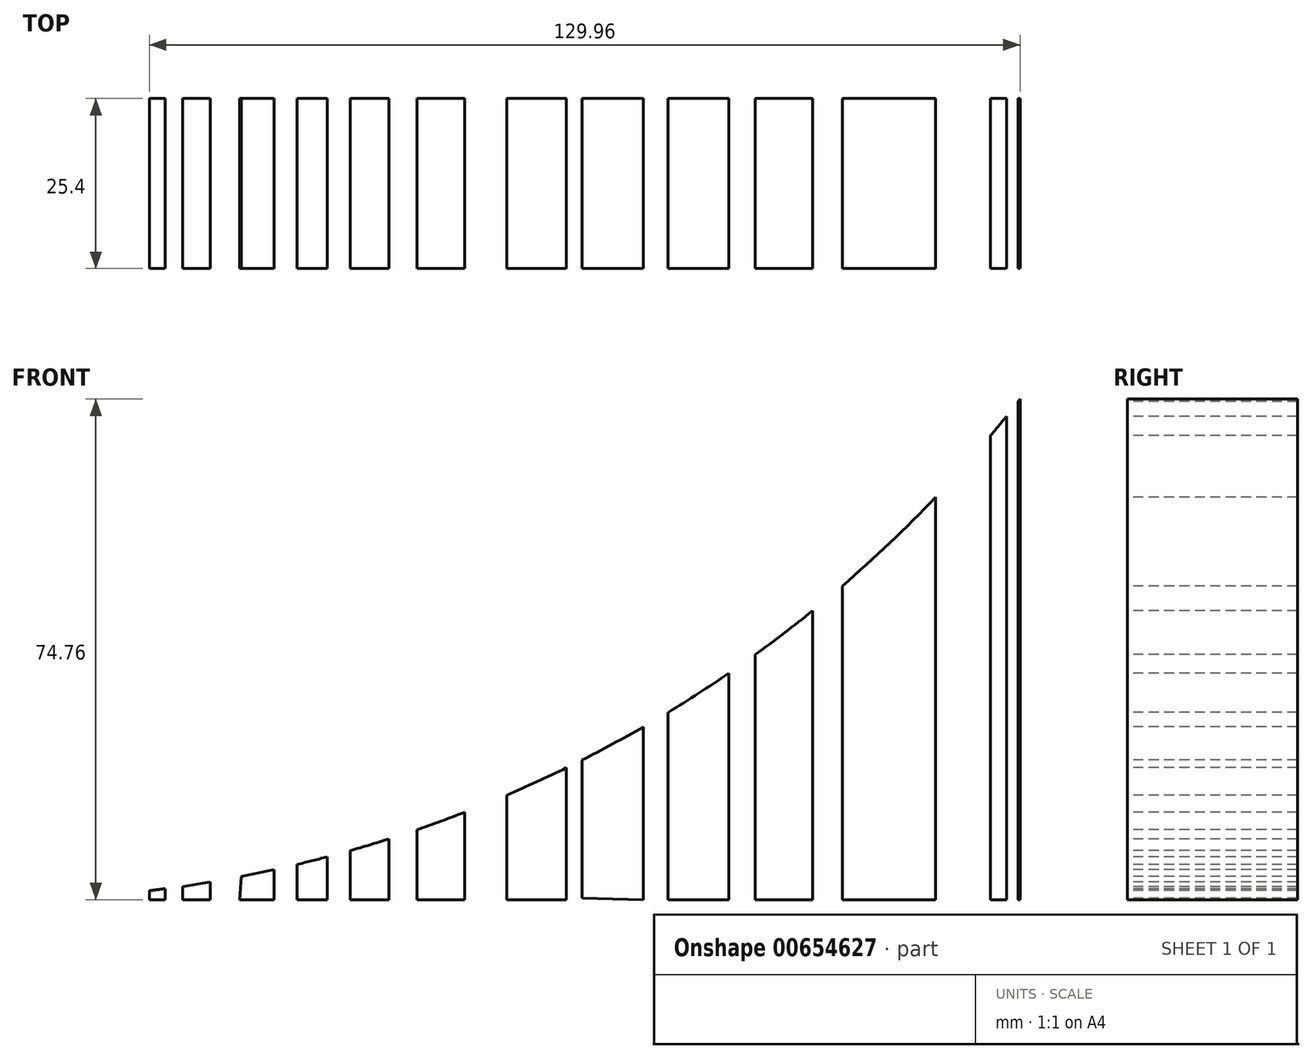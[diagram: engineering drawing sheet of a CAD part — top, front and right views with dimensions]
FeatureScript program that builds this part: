
annotation { "Feature Type Name" : "Feature", "Feature Type Description" : "" }
export const myFeature = defineFeature(function(context is Context, id is Id, definition is map)
    precondition{}
    {
        {
            var Q0;
            Q0=qCreatedBy(makeId("Front.planeOp"),FACE);
            var sketch = newSketch(context, id + "F0", { "sketchPlane" : qUnion([Q0])});
            skLineSegment(sketch, "E0", {"start": v(-76.13, -17.67) * mm, "end": v(76.6, -17.67) * mm});
            skLineSegment(sketch, "E1", {"start": v(76.6, -17.67) * mm, "end": v(76.6, 57.09) * mm});
            skArc(sketch, "E2", {"start": v(-76.13, -17.67) * mm, "mid": v(8.9, 2.02) * mm, "end": v(76.6, 57.09) * mm});
            skSolve(sketch);
        }
        {
            var Q0;
            Q0=makeQuery(id+"F0.imprint","IMPRINT",FACE,{"disambiguationData":[TD([[makeQuery(id+"F0.imprint","IMPRINT",EDGE,{"derivedFrom":sQuery(id+"F0.wireOp",EDGE,"E0")}),1.0]])]});
            extrude(context, id + "F1", {"entities" : qUnion([Q0]), "depth" : 25.4 * mm, "offsetDistance" : 25.4 * mm});
        }
        {
            var Q0;
            Q0=makeQuery(id+"F1.opExtrude","CAP_FACE",FACE,{"disambiguationData":[OSD([sQuery(id+"F0.wireOp",EDGE,"E0"),sQuery(id+"F0.wireOp",EDGE,"E1"),sQuery(id+"F0.wireOp",EDGE,"E2")])],"isStart":false});
            var sketch = newSketch(context, id + "F2", { "sketchPlane" : qUnion([Q0])});
            skLineSegment(sketch, "E3", {"start": v(76.3, 56.71) * mm, "end": v(76.3, -17.67) * mm});
            skLineSegment(sketch, "E4", {"start": v(76.3, -17.67) * mm, "end": v(74.56, -17.67) * mm});
            skLineSegment(sketch, "E5", {"start": v(74.56, -17.67) * mm, "end": v(74.56, 54.51) * mm});
            skLineSegment(sketch, "E6", {"start": v(74.56, 54.51) * mm, "end": v(76.3, 56.71) * mm});
            skLineSegment(sketch, "E7", {"start": v(72.2, 51.63) * mm, "end": v(72.2, -17.67) * mm});
            skLineSegment(sketch, "E8", {"start": v(72.2, -17.67) * mm, "end": v(64, -17.67) * mm});
            skLineSegment(sketch, "E9", {"start": v(64, -17.67) * mm, "end": v(64, 42.45) * mm});
            skLineSegment(sketch, "E10", {"start": v(64, 42.45) * mm, "end": v(65.31, 43.96) * mm});
            skLineSegment(sketch, "E11", {"start": v(50.05, 29.17) * mm, "end": v(50.05, -17.67) * mm});
            skLineSegment(sketch, "E12", {"start": v(50.05, -17.67) * mm, "end": v(48.52, -17.67) * mm});
            skLineSegment(sketch, "E13", {"start": v(48.52, -17.67) * mm, "end": v(48.52, 27.87) * mm});
            skLineSegment(sketch, "E14", {"start": v(48.52, 27.87) * mm, "end": v(50.05, 29.17) * mm});
            skLineSegment(sketch, "E15", {"start": v(45.66, 25.5) * mm, "end": v(45.66, -17.67) * mm});
            skLineSegment(sketch, "E16", {"start": v(45.66, -17.67) * mm, "end": v(37.08, -17.67) * mm});
            skLineSegment(sketch, "E17", {"start": v(37.08, -17.67) * mm, "end": v(37.08, 18.93) * mm});
            skLineSegment(sketch, "E18", {"start": v(37.08, 18.93) * mm, "end": v(45.66, 25.5) * mm});
            skLineSegment(sketch, "E19", {"start": v(33.12, 16.15) * mm, "end": v(33.12, -17.67) * mm});
            skLineSegment(sketch, "E20", {"start": v(33.12, -17.67) * mm, "end": v(24.07, -17.67) * mm});
            skLineSegment(sketch, "E21", {"start": v(24.07, -17.67) * mm, "end": v(24.07, 10.32) * mm});
            skLineSegment(sketch, "E22", {"start": v(24.07, 10.32) * mm, "end": v(33.12, 16.15) * mm});
            skLineSegment(sketch, "E23", {"start": v(20.35, 8.12) * mm, "end": v(20.35, -17.67) * mm});
            skLineSegment(sketch, "E24", {"start": v(20.35, -17.67) * mm, "end": v(11.2, -17.4) * mm});
            skLineSegment(sketch, "E25", {"start": v(11.2, -17.4) * mm, "end": v(11.2, 3.18) * mm});
            skLineSegment(sketch, "E26", {"start": v(11.2, 3.18) * mm, "end": v(20.25, 8.04) * mm});
            skLineSegment(sketch, "E27", {"start": v(8.9, 2.02) * mm, "end": v(8.9, -17.67) * mm});
            skPoint(sketch, "E27.endSnap0", {"position": v(8.9, 2.02) * mm});
            skLineSegment(sketch, "E28", {"start": v(8.9, -17.67) * mm, "end": v(0, -17.67) * mm});
            skLineSegment(sketch, "E29", {"start": v(0, -17.67) * mm, "end": v(0, -2.05) * mm});
            skLineSegment(sketch, "E30", {"start": v(0, -2.05) * mm, "end": v(8.9, 2.02) * mm});
            skLineSegment(sketch, "E31", {"start": v(-6.3, -4.62) * mm, "end": v(-6.3, -17.67) * mm});
            skLineSegment(sketch, "E32", {"start": v(-6.3, -17.67) * mm, "end": v(-13.44, -17.67) * mm});
            skLineSegment(sketch, "E33", {"start": v(-13.44, -17.67) * mm, "end": v(-13.44, -7.23) * mm});
            skLineSegment(sketch, "E34", {"start": v(-13.44, -7.23) * mm, "end": v(-6.3, -4.62) * mm});
            skLineSegment(sketch, "E35", {"start": v(-17.6, -8.6) * mm, "end": v(-17.6, -17.67) * mm});
            skLineSegment(sketch, "E36", {"start": v(-17.6, -17.67) * mm, "end": v(-23.43, -17.67) * mm});
            skLineSegment(sketch, "E37", {"start": v(-23.43, -17.67) * mm, "end": v(-23.43, -10.35) * mm});
            skLineSegment(sketch, "E38", {"start": v(-23.43, -10.35) * mm, "end": v(-17.6, -8.6) * mm});
            skLineSegment(sketch, "E39", {"start": v(-26.84, -11.28) * mm, "end": v(-26.84, -17.67) * mm});
            skLineSegment(sketch, "E40", {"start": v(-26.84, -17.67) * mm, "end": v(-31.33, -17.67) * mm});
            skLineSegment(sketch, "E41", {"start": v(-31.33, -17.67) * mm, "end": v(-31.33, -12.4) * mm});
            skLineSegment(sketch, "E42", {"start": v(-31.33, -12.4) * mm, "end": v(-26.84, -11.28) * mm});
            skLineSegment(sketch, "E43", {"start": v(-34.78, -13.2) * mm, "end": v(-34.78, -17.67) * mm});
            skLineSegment(sketch, "E44", {"start": v(-34.78, -17.67) * mm, "end": v(-39.89, -17.67) * mm});
            skLineSegment(sketch, "E45", {"start": v(-39.89, -17.67) * mm, "end": v(-39.63, -14.17) * mm});
            skLineSegment(sketch, "E46", {"start": v(-39.63, -14.17) * mm, "end": v(-34.78, -13.2) * mm});
            skLineSegment(sketch, "E47", {"start": v(-44.3, -15.03) * mm, "end": v(-44.3, -17.67) * mm});
            skLineSegment(sketch, "E48", {"start": v(-44.3, -17.67) * mm, "end": v(-48.45, -17.67) * mm});
            skLineSegment(sketch, "E49", {"start": v(-48.45, -17.67) * mm, "end": v(-48.45, -15.72) * mm});
            skLineSegment(sketch, "E50", {"start": v(-48.45, -15.72) * mm, "end": v(-44.3, -15.03) * mm});
            skLineSegment(sketch, "E51", {"start": v(-51, -16.03) * mm, "end": v(-51, -17.67) * mm});
            skLineSegment(sketch, "E52", {"start": v(-51, -17.67) * mm, "end": v(-53.37, -17.67) * mm});
            skLineSegment(sketch, "E53", {"start": v(-53.37, -17.67) * mm, "end": v(-53.37, -16.11) * mm});
            skLineSegment(sketch, "E54", {"start": v(-53.37, -16.11) * mm, "end": v(-51, -16.03) * mm});
            skSolve(sketch);
        }
        {
            var Q0;
            {var subQ0=sQuery(id+"F2.wireOp",EDGE,"E11");Q0=makeQuery(id+"F2.imprint","IMPRINT",FACE,{"disambiguationData":[TD([[makeQuery(id+"F2.imprint","IMPRINT",EDGE,{"derivedFrom":subQ0}),-1.0]])]});}
            var Q1;
            {var subQ0=sQuery(id+"F2.wireOp",EDGE,"E7");Q1=makeQuery(id+"F2.imprint","IMPRINT",FACE,{"disambiguationData":[TD([[makeQuery(id+"F2.imprint","IMPRINT",EDGE,{"derivedFrom":subQ0}),-1.0]])]});}
            var Q2;
            {var subQ0=sQuery(id+"F2.wireOp",EDGE,"E3");Q2=makeQuery(id+"F2.imprint","IMPRINT",FACE,{"disambiguationData":[TD([[makeQuery(id+"F2.imprint","IMPRINT",EDGE,{"derivedFrom":subQ0}),-1.0]])]});}
            var Q3;
            {var subQ0=sQuery(id+"F2.wireOp",EDGE,"E13");Q3=makeQuery(id+"F2.imprint","IMPRINT",FACE,{"disambiguationData":[TD([[makeQuery(id+"F2.imprint","IMPRINT",EDGE,{"derivedFrom":subQ0}),1.0]])]});}
            var Q4;
            {var subQ0=sQuery(id+"F2.wireOp",EDGE,"E17");Q4=makeQuery(id+"F2.imprint","IMPRINT",FACE,{"disambiguationData":[TD([[makeQuery(id+"F2.imprint","IMPRINT",EDGE,{"derivedFrom":subQ0}),1.0]])]});}
            var Q5;
            {var subQ0=sQuery(id+"F2.wireOp",EDGE,"E21");Q5=makeQuery(id+"F2.imprint","IMPRINT",FACE,{"disambiguationData":[TD([[makeQuery(id+"F2.imprint","IMPRINT",EDGE,{"derivedFrom":subQ0}),1.0]])]});}
            var Q6;
            {var subQ0=sQuery(id+"F2.wireOp",EDGE,"E24");Q6=makeQuery(id+"F2.imprint","IMPRINT",FACE,{"disambiguationData":[TD([[makeQuery(id+"F2.imprint","IMPRINT",EDGE,{"derivedFrom":subQ0}),1.0]])]});}
            var Q7;
            {var subQ0=sQuery(id+"F2.wireOp",EDGE,"E29");Q7=makeQuery(id+"F2.imprint","IMPRINT",FACE,{"disambiguationData":[TD([[makeQuery(id+"F2.imprint","IMPRINT",EDGE,{"derivedFrom":subQ0}),1.0]])]});}
            var Q8;
            {var subQ0=sQuery(id+"F2.wireOp",EDGE,"E33");Q8=makeQuery(id+"F2.imprint","IMPRINT",FACE,{"disambiguationData":[TD([[makeQuery(id+"F2.imprint","IMPRINT",EDGE,{"derivedFrom":subQ0}),1.0]])]});}
            var Q9;
            {var subQ5=sQuery(id+"F2.wireOp",EDGE,"E39");Q9=makeQuery(id+"F2.imprint","IMPRINT",FACE,{"disambiguationData":[TD([[makeQuery(id+"F2.imprint","IMPRINT",EDGE,{"derivedFrom":subQ5}),1.0]])]});}
            var Q10;
            {var subQ0=sQuery(id+"F2.wireOp",EDGE,"E41");Q10=makeQuery(id+"F2.imprint","IMPRINT",FACE,{"disambiguationData":[TD([[makeQuery(id+"F2.imprint","IMPRINT",EDGE,{"derivedFrom":subQ0}),1.0]])]});}
            var Q11;
            {var subQ5=sQuery(id+"F2.wireOp",EDGE,"E47");Q11=makeQuery(id+"F2.imprint","IMPRINT",FACE,{"disambiguationData":[TD([[makeQuery(id+"F2.imprint","IMPRINT",EDGE,{"derivedFrom":subQ5}),1.0]])]});}
            var Q12;
            {var subQ3=sQuery(id+"F2.wireOp",EDGE,"E49");Q12=makeQuery(id+"F2.imprint","IMPRINT",FACE,{"disambiguationData":[TD([[makeQuery(id+"F2.imprint","IMPRINT",EDGE,{"derivedFrom":subQ3}),1.0]])]});}
            var Q13;
            {var subQ1=makeQuery(id+"F1.opExtrude","CAP_EDGE",EDGE,{"disambiguationData":[OSD([sQuery(id+"F0.wireOp",EDGE,"E0")])],"isStart":false});var subQ3=makeQuery(id+"F1.opExtrude","CAP_EDGE",EDGE,{"disambiguationData":[OSD([sQuery(id+"F0.wireOp",EDGE,"E2")])],"isStart":false});var subQ5=makeQuery(id+"F2.imprint","INTERSECT",VERTEX,{"derivedFrom":[subQ1,subQ3]});Q13=makeQuery(id+"F2.imprint","IMPRINT",FACE,{"disambiguationData":[TD([[makeQuery(id+"F2.imprint","IMPRINT",EDGE,{"disambiguationData":[TD([[subQ5,-1.0]])],"derivedFrom":subQ3}),-1.0]])]});}
            extrude(context, id + "F3", {"entities" : qUnion([Q0, Q1, Q2, Q3, Q4, Q5, Q6, Q7, Q8, Q9, Q10, Q11, Q12, Q13]), "operationType" : NewBodyOperationType.REMOVE, "oppositeDirection" : true, "depth" : 25.4 * mm, "offsetDistance" : 25.4 * mm});
        }
    });
